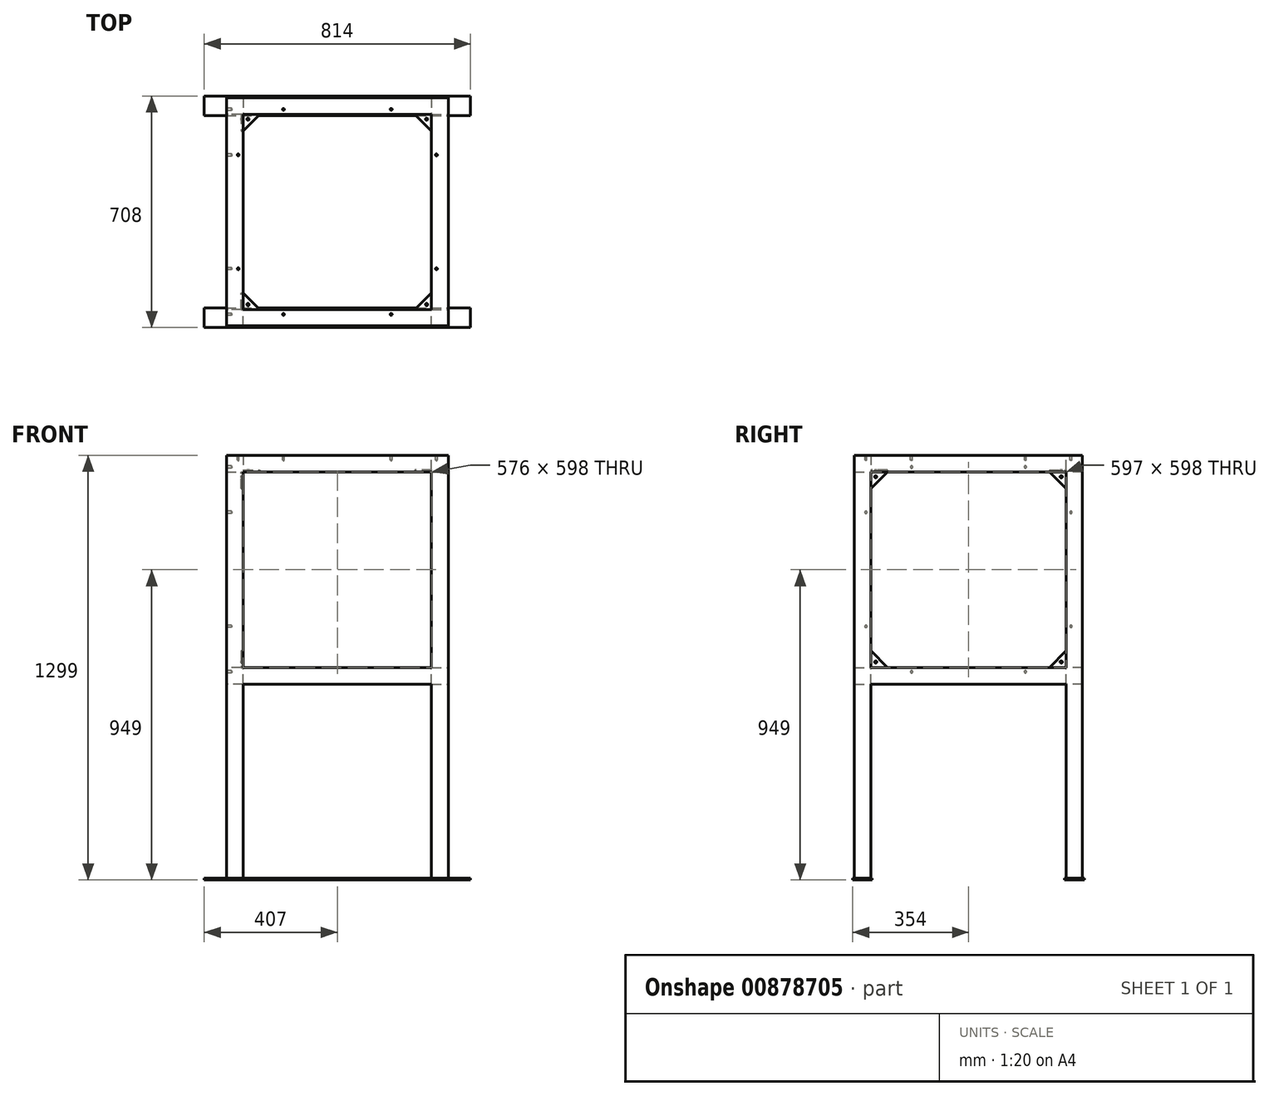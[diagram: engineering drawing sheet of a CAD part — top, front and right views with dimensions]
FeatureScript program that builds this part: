
annotation { "Feature Type Name" : "Feature", "Feature Type Description" : "" }
export const myFeature = defineFeature(function(context is Context, id is Id, definition is map)
    precondition{}
    {
        {
            var Q0;
            Q0=qCreatedBy(makeId("Front.planeOp"),FACE);
            var sketch = newSketch(context, id + "F0", { "sketchPlane" : qUnion([Q0])});
            skLineSegment(sketch, "E0.bottom", {"start": v(0, 0) * mm, "end": v(678, 0) * mm});
            skLineSegment(sketch, "E0.top", {"start": v(51, -51) * mm, "end": v(627, -51) * mm});
            skLineSegment(sketch, "E0.left", {"start": v(0, 0) * mm, "end": v(0, -51) * mm});
            skLineSegment(sketch, "E0.right", {"start": v(678, 0) * mm, "end": v(678, -51) * mm});
            skLineSegment(sketch, "E1.bottom", {"start": v(0, 0) * mm, "end": v(51, 0) * mm});
            skLineSegment(sketch, "E1.top", {"start": v(0, -1294) * mm, "end": v(51, -1294) * mm});
            skLineSegment(sketch, "E1.left", {"start": v(0, 0) * mm, "end": v(0, -1294) * mm});
            skLineSegment(sketch, "E1.right", {"start": v(51, -51) * mm, "end": v(51, -649) * mm});
            skLineSegment(sketch, "E2.bottom", {"start": v(678, 0) * mm, "end": v(627, 0) * mm});
            skLineSegment(sketch, "E2.top", {"start": v(678, -1294) * mm, "end": v(627, -1294) * mm});
            skLineSegment(sketch, "E2.left", {"start": v(678, 0) * mm, "end": v(678, -1294) * mm});
            skLineSegment(sketch, "E2.right", {"start": v(627, -51) * mm, "end": v(627, -649) * mm});
            skLineSegment(sketch, "E3.bottom", {"start": v(51, -649) * mm, "end": v(627, -649) * mm});
            skLineSegment(sketch, "E3.top", {"start": v(51, -700) * mm, "end": v(627, -700) * mm});
            skLineSegment(sketch, "E3.left", {"start": v(0, -649) * mm, "end": v(0, -700) * mm});
            skLineSegment(sketch, "E3.right", {"start": v(678, -649) * mm, "end": v(678, -700) * mm});
            skLineSegment(sketch, "E4.trimOffspring", {"start": v(627, -700) * mm, "end": v(627, -1294) * mm});
            skLineSegment(sketch, "E5.trimOffspring", {"start": v(51, -700) * mm, "end": v(51, -1294) * mm});
            skSolve(sketch);
        }
        {
            var Q0;
            Q0 = qSketchRegion(id + "F0", true);
            extrude(context, id + "F1", {"entities" : qUnion([Q0]), "depth" : 50.1 * mm, "offsetDistance" : 25 * mm});
        }
        {
            var Q0;
            Q0=qCreatedBy(makeId("Front.planeOp"),FACE);
            cPlane(context, id + "F2", {"entities" : qUnion([Q0]), "cplaneType" : CPlaneType.OFFSET, "offset" : 298.5 * mm, "oppositeDirection" : true, "width" : 150 * mm, "height" : 150 * mm});
        }
        {
            var Q0;
            Q0=makeQuery(id+"F1.opExtrude","CAP_FACE",FACE,{"disambiguationData":[OSD([sQuery(id+"F0.wireOp",EDGE,"E0.bottom"),sQuery(id+"F0.wireOp",EDGE,"E0.top"),sQuery(id+"F0.wireOp",EDGE,"E1.bottom"),sQuery(id+"F0.wireOp",EDGE,"E1.top"),sQuery(id+"F0.wireOp",EDGE,"E1.left"),sQuery(id+"F0.wireOp",EDGE,"E1.right"),sQuery(id+"F0.wireOp",EDGE,"E2.bottom"),sQuery(id+"F0.wireOp",EDGE,"E2.top"),sQuery(id+"F0.wireOp",EDGE,"E2.left"),sQuery(id+"F0.wireOp",EDGE,"E2.right"),sQuery(id+"F0.wireOp",EDGE,"E3.bottom"),sQuery(id+"F0.wireOp",EDGE,"E3.top"),sQuery(id+"F0.wireOp",EDGE,"E3.left"),sQuery(id+"F0.wireOp",EDGE,"E3.right"),sQuery(id+"F0.wireOp",EDGE,"E4.trimOffspring"),sQuery(id+"F0.wireOp",EDGE,"E5.trimOffspring")])],"isStart":true});
            var sketch = newSketch(context, id + "F3", { "sketchPlane" : qUnion([Q0])});
            skLineSegment(sketch, "E6.bottom", {"start": v(0, 0) * mm, "end": v(-51, 0) * mm});
            skLineSegment(sketch, "E6.top", {"start": v(0, -51) * mm, "end": v(-51, -51) * mm});
            skLineSegment(sketch, "E6.left", {"start": v(0, 0) * mm, "end": v(0, -51) * mm});
            skLineSegment(sketch, "E6.right", {"start": v(-51, 0) * mm, "end": v(-51, -51) * mm});
            skLineSegment(sketch, "E7.bottom", {"start": v(-627, -51) * mm, "end": v(-678, -51) * mm});
            skLineSegment(sketch, "E7.top", {"start": v(-627, 0) * mm, "end": v(-678, 0) * mm});
            skLineSegment(sketch, "E7.left", {"start": v(-627, -51) * mm, "end": v(-627, 0) * mm});
            skLineSegment(sketch, "E7.right", {"start": v(-678, -51) * mm, "end": v(-678, 0) * mm});
            skLineSegment(sketch, "E8.bottom", {"start": v(-627, -700) * mm, "end": v(-678, -700) * mm});
            skLineSegment(sketch, "E8.top", {"start": v(-627, -649) * mm, "end": v(-678, -649) * mm});
            skLineSegment(sketch, "E8.left", {"start": v(-627, -700) * mm, "end": v(-627, -649) * mm});
            skLineSegment(sketch, "E8.right", {"start": v(-678, -700) * mm, "end": v(-678, -649) * mm});
            skLineSegment(sketch, "E9.bottom", {"start": v(-51, -700) * mm, "end": v(0, -700) * mm});
            skLineSegment(sketch, "E9.top", {"start": v(-51, -649) * mm, "end": v(0, -649) * mm});
            skLineSegment(sketch, "E9.left", {"start": v(-51, -700) * mm, "end": v(-51, -649) * mm});
            skLineSegment(sketch, "E9.right", {"start": v(0, -700) * mm, "end": v(0, -649) * mm});
            skSolve(sketch);
        }
        {
            var Q0;
            Q0 = qSketchRegion(id + "F3", true);
            extrude(context, id + "F4", {"entities" : qUnion([Q0]), "operationType" : NewBodyOperationType.ADD, "depth" : 298.5 * mm, "offsetDistance" : 25 * mm});
        }
        {
            var Q0;
            Q0=makeQuery(id+"F1.opExtrude","SWEPT_BODY",BODY,{"disambiguationData":[OSD([sQuery(id+"F0.wireOp",EDGE,"E0.bottom"),sQuery(id+"F0.wireOp",EDGE,"E0.top"),sQuery(id+"F0.wireOp",EDGE,"E1.bottom"),sQuery(id+"F0.wireOp",EDGE,"E1.top"),sQuery(id+"F0.wireOp",EDGE,"E1.left"),sQuery(id+"F0.wireOp",EDGE,"E1.right"),sQuery(id+"F0.wireOp",EDGE,"E2.bottom"),sQuery(id+"F0.wireOp",EDGE,"E2.top"),sQuery(id+"F0.wireOp",EDGE,"E2.left"),sQuery(id+"F0.wireOp",EDGE,"E2.right"),sQuery(id+"F0.wireOp",EDGE,"E3.bottom"),sQuery(id+"F0.wireOp",EDGE,"E3.top"),sQuery(id+"F0.wireOp",EDGE,"E3.left"),sQuery(id+"F0.wireOp",EDGE,"E3.right"),sQuery(id+"F0.wireOp",EDGE,"E4.trimOffspring"),sQuery(id+"F0.wireOp",EDGE,"E5.trimOffspring")])]});
            var Q1;
            Q1=qCreatedBy(id+"F2.planeOp",FACE);
            mirror(context, id + "F5", {"operationType" : NewBodyOperationType.ADD, "entities" : qUnion([Q0]), "mirrorPlane" : qUnion([Q1])});
        }
        {
            var Q0;
            Q0=qCreatedBy(makeId("Top.planeOp"),FACE);
            cPlane(context, id + "F6", {"entities" : qUnion([Q0]), "cplaneType" : CPlaneType.OFFSET, "offset" : 50.1 * mm, "oppositeDirection" : true, "width" : 150 * mm, "height" : 150 * mm});
        }
        {
            var Q0;
            Q0=qCreatedBy(id+"F6.planeOp",FACE);
            var sketch = newSketch(context, id + "F7", { "sketchPlane" : qUnion([Q0])});
            skLineSegment(sketch, "E10", {"start": v(102, 0) * mm, "end": v(51, 51) * mm});
            skLineSegment(sketch, "E11", {"start": v(51, 51) * mm, "end": v(51, 0) * mm});
            skLineSegment(sketch, "E12", {"start": v(51, 0) * mm, "end": v(102, 0) * mm});
            skLineSegment(sketch, "E13.MirrorCS", {"start": v(51, 546) * mm, "end": v(51, 597) * mm});
            skLineSegment(sketch, "E14.MirrorCS", {"start": v(102, 597) * mm, "end": v(51, 546) * mm});
            skLineSegment(sketch, "E15.MirrorCS", {"start": v(51, 597) * mm, "end": v(102, 597) * mm});
            skLineSegment(sketch, "E16", {"start": v(339, -108.34) * mm, "end": v(339, 683.5) * mm, "construction": true});
            skLineSegment(sketch, "E17.MirrorCS", {"start": v(627, 546) * mm, "end": v(627, 597) * mm});
            skLineSegment(sketch, "E18.MirrorCS", {"start": v(627, 597) * mm, "end": v(576, 597) * mm});
            skLineSegment(sketch, "E19.MirrorCS", {"start": v(576, 597) * mm, "end": v(627, 546) * mm});
            skLineSegment(sketch, "E20.MirrorCS", {"start": v(627, 51) * mm, "end": v(627, 0) * mm});
            skLineSegment(sketch, "E21.MirrorCS", {"start": v(627, 0) * mm, "end": v(576, 0) * mm});
            skLineSegment(sketch, "E22.MirrorCS", {"start": v(576, 0) * mm, "end": v(627, 51) * mm});
            skSolve(sketch);
        }
        {
            var Q0;
            Q0 = qSketchRegion(id + "F7", true);
            extrude(context, id + "F8", {"entities" : qUnion([Q0]), "operationType" : NewBodyOperationType.ADD, "depth" : 5 * mm, "offsetDistance" : 25 * mm});
        }
        {
            var Q0;
            Q0=qCreatedBy(makeId("Right.planeOp"),FACE);
            cPlane(context, id + "F9", {"entities" : qUnion([Q0]), "cplaneType" : CPlaneType.OFFSET, "offset" : 50.1 * mm, "width" : 150 * mm, "height" : 150 * mm});
        }
        {
            var Q0;
            Q0=qCreatedBy(id+"F9.planeOp",FACE);
            var sketch = newSketch(context, id + "F10", { "sketchPlane" : qUnion([Q0])});
            skLineSegment(sketch, "E23", {"start": v(0, -51) * mm, "end": v(51, -51) * mm});
            skLineSegment(sketch, "E24", {"start": v(51, -51) * mm, "end": v(0, -102) * mm});
            skLineSegment(sketch, "E25", {"start": v(0, -102) * mm, "end": v(0, -51) * mm});
            skLineSegment(sketch, "E26.MirrorCS", {"start": v(597, -102) * mm, "end": v(597, -51) * mm});
            skLineSegment(sketch, "E27.MirrorCS", {"start": v(546, -51) * mm, "end": v(597, -102) * mm});
            skLineSegment(sketch, "E28.MirrorCS", {"start": v(597, -51) * mm, "end": v(546, -51) * mm});
            skLineSegment(sketch, "E29", {"start": v(-148.3, -350) * mm, "end": v(735.3, -350) * mm, "construction": true});
            skLineSegment(sketch, "E30.MirrorCS", {"start": v(51, -649) * mm, "end": v(0, -598) * mm});
            skLineSegment(sketch, "E31.MirrorCS", {"start": v(0, -598) * mm, "end": v(0, -649) * mm});
            skLineSegment(sketch, "E32.MirrorCS", {"start": v(0, -649) * mm, "end": v(51, -649) * mm});
            skLineSegment(sketch, "E33.MirrorCS", {"start": v(546, -649) * mm, "end": v(597, -598) * mm});
            skLineSegment(sketch, "E34.MirrorCS", {"start": v(597, -598) * mm, "end": v(597, -649) * mm});
            skLineSegment(sketch, "E35.MirrorCS", {"start": v(597, -649) * mm, "end": v(546, -649) * mm});
            skSolve(sketch);
        }
        {
            var Q0;
            Q0=qCreatedBy(id+"F6.planeOp",FACE);
            cPlane(context, id + "F11", {"entities" : qUnion([Q0]), "cplaneType" : CPlaneType.OFFSET, "offset" : 299 * mm, "oppositeDirection" : true, "width" : 150 * mm, "height" : 150 * mm});
        }
        {
            var Q0;
            Q0 = qSketchRegion(id + "F10", true);
            extrude(context, id + "F12", {"entities" : qUnion([Q0]), "operationType" : NewBodyOperationType.ADD, "oppositeDirection" : true, "depth" : 5 * mm, "offsetDistance" : 25 * mm});
        }
        {
            var Q0;
            Q0=makeQuery(id+"F1.opExtrude","SWEPT_FACE",FACE,{"disambiguationData":[OSD([sQuery(id+"F0.wireOp",EDGE,"E1.top")])]});
            var sketch = newSketch(context, id + "F13", { "sketchPlane" : qUnion([Q0])});
            skLineSegment(sketch, "E36.bottom", {"start": v(-68, 55.5) * mm, "end": v(746, 55.5) * mm});
            skLineSegment(sketch, "E36.top", {"start": v(-68, -4.5) * mm, "end": v(746, -4.5) * mm});
            skLineSegment(sketch, "E36.left", {"start": v(-68, 55.5) * mm, "end": v(-68, -4.5) * mm});
            skLineSegment(sketch, "E36.right", {"start": v(746, 55.5) * mm, "end": v(746, -4.5) * mm});
            skLineSegment(sketch, "E37.MirrorCS", {"start": v(-68, -652.5) * mm, "end": v(-68, -592.5) * mm});
            skLineSegment(sketch, "E38.MirrorCS", {"start": v(-68, -652.5) * mm, "end": v(746, -652.5) * mm});
            skLineSegment(sketch, "E39.MirrorCS", {"start": v(-68, -592.5) * mm, "end": v(746, -592.5) * mm});
            skLineSegment(sketch, "E40.MirrorCS", {"start": v(746, -652.5) * mm, "end": v(746, -592.5) * mm});
            skSolve(sketch);
        }
        {
            var Q0;
            Q0 = qSketchRegion(id + "F13", true);
            extrude(context, id + "F14", {"entities" : qUnion([Q0]), "operationType" : NewBodyOperationType.ADD, "depth" : 5 * mm, "offsetDistance" : 25 * mm});
        }
        {
            var Q0;
            Q0=makeQuery(id+"F8.opExtrude","CAP_FACE",FACE,{"disambiguationData":[OSD([sQuery(id+"F7.wireOp",EDGE,"E10"),sQuery(id+"F7.wireOp",EDGE,"E11"),sQuery(id+"F7.wireOp",EDGE,"E12")])],"isStart":false});
            var sketch = newSketch(context, id + "F15", { "sketchPlane" : qUnion([Q0])});
            skCircle(sketch, "E41", {"center": v(66, 15) * mm, "radius": 3.5 * mm});
            skCircle(sketch, "E42.MirrorC", {"center": v(66, 582) * mm, "radius": 3.5 * mm});
            skLineSegment(sketch, "E43", {"start": v(339, -97.85) * mm, "end": v(339, 673.8) * mm, "construction": true});
            skCircle(sketch, "E44.MirrorC", {"center": v(612, 582) * mm, "radius": 3.5 * mm});
            skCircle(sketch, "E45.MirrorC", {"center": v(612, 15) * mm, "radius": 3.5 * mm});
            skSolve(sketch);
        }
        {
            var Q0;
            Q0=sQuery(id+"F15.wireOp",VERTEX,"E42.MirrorC.center");
            var Q1;
            Q1=sQuery(id+"F15.wireOp",VERTEX,"E44.MirrorC.center");
            var Q2;
            Q2=sQuery(id+"F15.wireOp",VERTEX,"E45.MirrorC.center");
            var Q3;
            Q3=sQuery(id+"F15.wireOp",VERTEX,"E41.center");
            var Q4;
            Q4=makeQuery(id+"F1.opExtrude","SWEPT_BODY",BODY,{"disambiguationData":[OSD([sQuery(id+"F0.wireOp",EDGE,"E0.bottom"),sQuery(id+"F0.wireOp",EDGE,"E0.top"),sQuery(id+"F0.wireOp",EDGE,"E1.bottom"),sQuery(id+"F0.wireOp",EDGE,"E1.top"),sQuery(id+"F0.wireOp",EDGE,"E1.left"),sQuery(id+"F0.wireOp",EDGE,"E1.right"),sQuery(id+"F0.wireOp",EDGE,"E2.bottom"),sQuery(id+"F0.wireOp",EDGE,"E2.top"),sQuery(id+"F0.wireOp",EDGE,"E2.left"),sQuery(id+"F0.wireOp",EDGE,"E2.right"),sQuery(id+"F0.wireOp",EDGE,"E3.bottom"),sQuery(id+"F0.wireOp",EDGE,"E3.top"),sQuery(id+"F0.wireOp",EDGE,"E3.left"),sQuery(id+"F0.wireOp",EDGE,"E3.right"),sQuery(id+"F0.wireOp",EDGE,"E4.trimOffspring"),sQuery(id+"F0.wireOp",EDGE,"E5.trimOffspring")])]});
            hole(context, id + "F16", {"style" : HoleStyle.SIMPLE, "endStyle" : HoleEndStyle.THROUGH, "holeDiameter" : 7 * mm, "majorDiameter" : 5 * mm, "isTappedThrough" : true, "tappedDepth" : 12 * mm, "tapClearance" : 3, "locations" : qUnion([Q0, Q1, Q2, Q3]), "scope" : qUnion([Q4])});
        }
        {
            var Q0;
            Q0=makeQuery(id+"F12.opExtrude","CAP_FACE",FACE,{"disambiguationData":[OSD([sQuery(id+"F10.wireOp",EDGE,"E23"),sQuery(id+"F10.wireOp",EDGE,"E24"),sQuery(id+"F10.wireOp",EDGE,"E25")])],"isStart":true});
            var sketch = newSketch(context, id + "F17", { "sketchPlane" : qUnion([Q0])});
            skCircle(sketch, "E46", {"center": v(15, -66) * mm, "radius": 3.5 * mm});
            skCircle(sketch, "E47.MirrorC", {"center": v(582, -66) * mm, "radius": 3.5 * mm});
            skCircle(sketch, "E48.MirrorC", {"center": v(15, -632.2) * mm, "radius": 3.5 * mm});
            skCircle(sketch, "E49.MirrorC", {"center": v(582, -632.2) * mm, "radius": 3.5 * mm});
            skSolve(sketch);
        }
        {
            var Q0;
            Q0=sQuery(id+"F17.wireOp",VERTEX,"E48.MirrorC.center");
            var Q1;
            Q1=sQuery(id+"F17.wireOp",VERTEX,"E49.MirrorC.center");
            var Q2;
            Q2=sQuery(id+"F17.wireOp",VERTEX,"E47.MirrorC.center");
            var Q3;
            Q3=sQuery(id+"F17.wireOp",VERTEX,"E46.center");
            var Q4;
            Q4=makeQuery(id+"F1.opExtrude","SWEPT_BODY",BODY,{"disambiguationData":[OSD([sQuery(id+"F0.wireOp",EDGE,"E0.bottom"),sQuery(id+"F0.wireOp",EDGE,"E0.top"),sQuery(id+"F0.wireOp",EDGE,"E1.bottom"),sQuery(id+"F0.wireOp",EDGE,"E1.top"),sQuery(id+"F0.wireOp",EDGE,"E1.left"),sQuery(id+"F0.wireOp",EDGE,"E1.right"),sQuery(id+"F0.wireOp",EDGE,"E2.bottom"),sQuery(id+"F0.wireOp",EDGE,"E2.top"),sQuery(id+"F0.wireOp",EDGE,"E2.left"),sQuery(id+"F0.wireOp",EDGE,"E2.right"),sQuery(id+"F0.wireOp",EDGE,"E3.bottom"),sQuery(id+"F0.wireOp",EDGE,"E3.top"),sQuery(id+"F0.wireOp",EDGE,"E3.left"),sQuery(id+"F0.wireOp",EDGE,"E3.right"),sQuery(id+"F0.wireOp",EDGE,"E4.trimOffspring"),sQuery(id+"F0.wireOp",EDGE,"E5.trimOffspring")])]});
            hole(context, id + "F18", {"style" : HoleStyle.SIMPLE, "endStyle" : HoleEndStyle.THROUGH, "holeDiameter" : 7 * mm, "majorDiameter" : 5 * mm, "isTappedThrough" : true, "tappedDepth" : 12 * mm, "tapClearance" : 3, "locations" : qUnion([Q0, Q1, Q2, Q3]), "scope" : qUnion([Q4])});
        }
        {
            var Q0;
            {var subQ0=makeQuery(id+"F4.boolean.opBoolean","MERGE",FACE,{"derivedFrom":[makeQuery(id+"F1.opExtrude","SWEPT_FACE",FACE,{"disambiguationData":[OSD([sQuery(id+"F0.wireOp",EDGE,"E1.left"),sQuery(id+"F0.wireOp",EDGE,"E3.left")])]}),makeQuery(id+"F4.opExtrude","SWEPT_FACE",FACE,{"disambiguationData":[OSD([sQuery(id+"F3.wireOp",EDGE,"E6.left")])]}),makeQuery(id+"F4.opExtrude","SWEPT_FACE",FACE,{"disambiguationData":[OSD([sQuery(id+"F3.wireOp",EDGE,"E9.right")])]})]});Q0=makeQuery(id+"F5.boolean.opBoolean","MERGE",FACE,{"derivedFrom":[subQ0,makeQuery(id+"F5.opPattern","COPY",FACE,{"derivedFrom":subQ0,"instanceName":"1"})]});}
            var sketch = newSketch(context, id + "F19", { "sketchPlane" : qUnion([Q0])});
            skCircle(sketch, "E50", {"center": v(-124.65, -36) * mm, "radius": 3 * mm});
            skCircle(sketch, "E51", {"center": v(15, -174.75) * mm, "radius": 3 * mm});
            skCircle(sketch, "E52.MirrorC", {"center": v(-472.35, -36) * mm, "radius": 3 * mm});
            skCircle(sketch, "E53.MirrorC", {"center": v(-612, -174.75) * mm, "radius": 3 * mm});
            skCircle(sketch, "E54.MirrorC", {"center": v(-612, -523.45) * mm, "radius": 3 * mm});
            skCircle(sketch, "E55.MirrorC", {"center": v(-472.35, -662.2) * mm, "radius": 3 * mm});
            skCircle(sketch, "E56.MirrorC", {"center": v(-124.65, -662.2) * mm, "radius": 3 * mm});
            skCircle(sketch, "E57.MirrorC", {"center": v(15, -523.45) * mm, "radius": 3 * mm});
            skSolve(sketch);
        }
        {
            var Q0;
            Q0=sQuery(id+"F19.wireOp",VERTEX,"E53.MirrorC.center");
            var Q1;
            Q1=sQuery(id+"F19.wireOp",VERTEX,"E52.MirrorC.center");
            var Q2;
            Q2=sQuery(id+"F19.wireOp",VERTEX,"E50.center");
            var Q3;
            Q3=sQuery(id+"F19.wireOp",VERTEX,"E51.center");
            var Q4;
            Q4=sQuery(id+"F19.wireOp",VERTEX,"E57.MirrorC.center");
            var Q5;
            Q5=sQuery(id+"F19.wireOp",VERTEX,"E56.MirrorC.center");
            var Q6;
            Q6=sQuery(id+"F19.wireOp",VERTEX,"E55.MirrorC.center");
            var Q7;
            Q7=sQuery(id+"F19.wireOp",VERTEX,"E54.MirrorC.center");
            var Q8;
            Q8=makeQuery(id+"F1.opExtrude","SWEPT_BODY",BODY,{"disambiguationData":[OSD([sQuery(id+"F0.wireOp",EDGE,"E0.bottom"),sQuery(id+"F0.wireOp",EDGE,"E0.top"),sQuery(id+"F0.wireOp",EDGE,"E1.bottom"),sQuery(id+"F0.wireOp",EDGE,"E1.top"),sQuery(id+"F0.wireOp",EDGE,"E1.left"),sQuery(id+"F0.wireOp",EDGE,"E1.right"),sQuery(id+"F0.wireOp",EDGE,"E2.bottom"),sQuery(id+"F0.wireOp",EDGE,"E2.top"),sQuery(id+"F0.wireOp",EDGE,"E2.left"),sQuery(id+"F0.wireOp",EDGE,"E2.right"),sQuery(id+"F0.wireOp",EDGE,"E3.bottom"),sQuery(id+"F0.wireOp",EDGE,"E3.top"),sQuery(id+"F0.wireOp",EDGE,"E3.left"),sQuery(id+"F0.wireOp",EDGE,"E3.right"),sQuery(id+"F0.wireOp",EDGE,"E4.trimOffspring"),sQuery(id+"F0.wireOp",EDGE,"E5.trimOffspring")])]});
            hole(context, id + "F20", {"style" : HoleStyle.SIMPLE, "endStyle" : HoleEndStyle.BLIND, "holeDiameter" : 7 * mm, "majorDiameter" : 5 * mm, "holeDepth" : 15 * mm, "isTappedThrough" : true, "tappedDepth" : 12 * mm, "tapClearance" : 3, "locations" : qUnion([Q0, Q1, Q2, Q3, Q4, Q5, Q6, Q7]), "scope" : qUnion([Q8])});
        }
        {
            var Q0;
            Q0=qCreatedBy(makeId("Right.planeOp"),FACE);
            cPlane(context, id + "F21", {"entities" : qUnion([Q0]), "cplaneType" : CPlaneType.OFFSET, "offset" : 339 * mm, "width" : 150 * mm, "height" : 150 * mm});
        }
        {
            var Q0;
            {var subQ0=makeQuery(id+"F4.boolean.opBoolean","MERGE",FACE,{"derivedFrom":[makeQuery(id+"F1.opExtrude","SWEPT_FACE",FACE,{"disambiguationData":[OSD([sQuery(id+"F0.wireOp",EDGE,"E0.bottom"),sQuery(id+"F0.wireOp",EDGE,"E1.bottom"),sQuery(id+"F0.wireOp",EDGE,"E2.bottom")])]}),makeQuery(id+"F4.opExtrude","SWEPT_FACE",FACE,{"disambiguationData":[OSD([sQuery(id+"F3.wireOp",EDGE,"E6.bottom")])]}),makeQuery(id+"F4.opExtrude","SWEPT_FACE",FACE,{"disambiguationData":[OSD([sQuery(id+"F3.wireOp",EDGE,"E7.top")])]})]});Q0=makeQuery(id+"F5.boolean.opBoolean","MERGE",FACE,{"derivedFrom":[subQ0,makeQuery(id+"F5.opPattern","COPY",FACE,{"derivedFrom":subQ0,"instanceName":"1"})]});}
            var sketch = newSketch(context, id + "F22", { "sketchPlane" : qUnion([Q0])});
            skCircle(sketch, "E58", {"center": v(36, 124.4) * mm, "radius": 3 * mm});
            skCircle(sketch, "E59", {"center": v(174.5, -15) * mm, "radius": 3 * mm});
            skCircle(sketch, "E60.MirrorC", {"center": v(36, 472.6) * mm, "radius": 3 * mm});
            skCircle(sketch, "E61.MirrorC", {"center": v(174.5, 612) * mm, "radius": 3 * mm});
            skCircle(sketch, "E62.MirrorC", {"center": v(503.5, -15) * mm, "radius": 3 * mm});
            skCircle(sketch, "E63.MirrorC", {"center": v(642, 124.4) * mm, "radius": 3 * mm});
            skCircle(sketch, "E64.MirrorC", {"center": v(642, 472.6) * mm, "radius": 3 * mm});
            skCircle(sketch, "E65.MirrorC", {"center": v(503.5, 612) * mm, "radius": 3 * mm});
            skSolve(sketch);
        }
        {
            var Q0;
            Q0=sQuery(id+"F22.wireOp",VERTEX,"E59.center");
            var Q1;
            Q1=sQuery(id+"F22.wireOp",VERTEX,"E58.center");
            var Q2;
            Q2=sQuery(id+"F22.wireOp",VERTEX,"E60.MirrorC.center");
            var Q3;
            Q3=sQuery(id+"F22.wireOp",VERTEX,"E61.MirrorC.center");
            var Q4;
            Q4=sQuery(id+"F22.wireOp",VERTEX,"E65.MirrorC.center");
            var Q5;
            Q5=sQuery(id+"F22.wireOp",VERTEX,"E64.MirrorC.center");
            var Q6;
            Q6=sQuery(id+"F22.wireOp",VERTEX,"E63.MirrorC.center");
            var Q7;
            Q7=sQuery(id+"F22.wireOp",VERTEX,"E62.MirrorC.center");
            var Q8;
            Q8=makeQuery(id+"F1.opExtrude","SWEPT_BODY",BODY,{"disambiguationData":[OSD([sQuery(id+"F0.wireOp",EDGE,"E0.bottom"),sQuery(id+"F0.wireOp",EDGE,"E0.top"),sQuery(id+"F0.wireOp",EDGE,"E1.bottom"),sQuery(id+"F0.wireOp",EDGE,"E1.top"),sQuery(id+"F0.wireOp",EDGE,"E1.left"),sQuery(id+"F0.wireOp",EDGE,"E1.right"),sQuery(id+"F0.wireOp",EDGE,"E2.bottom"),sQuery(id+"F0.wireOp",EDGE,"E2.top"),sQuery(id+"F0.wireOp",EDGE,"E2.left"),sQuery(id+"F0.wireOp",EDGE,"E2.right"),sQuery(id+"F0.wireOp",EDGE,"E3.bottom"),sQuery(id+"F0.wireOp",EDGE,"E3.top"),sQuery(id+"F0.wireOp",EDGE,"E3.left"),sQuery(id+"F0.wireOp",EDGE,"E3.right"),sQuery(id+"F0.wireOp",EDGE,"E4.trimOffspring"),sQuery(id+"F0.wireOp",EDGE,"E5.trimOffspring")])]});
            hole(context, id + "F23", {"style" : HoleStyle.SIMPLE, "endStyle" : HoleEndStyle.BLIND, "holeDiameter" : 6 * mm, "majorDiameter" : 5 * mm, "holeDepth" : 15 * mm, "isTappedThrough" : true, "tappedDepth" : 12 * mm, "tapClearance" : 3, "locations" : qUnion([Q0, Q1, Q2, Q3, Q4, Q5, Q6, Q7]), "scope" : qUnion([Q8])});
        }
    });
